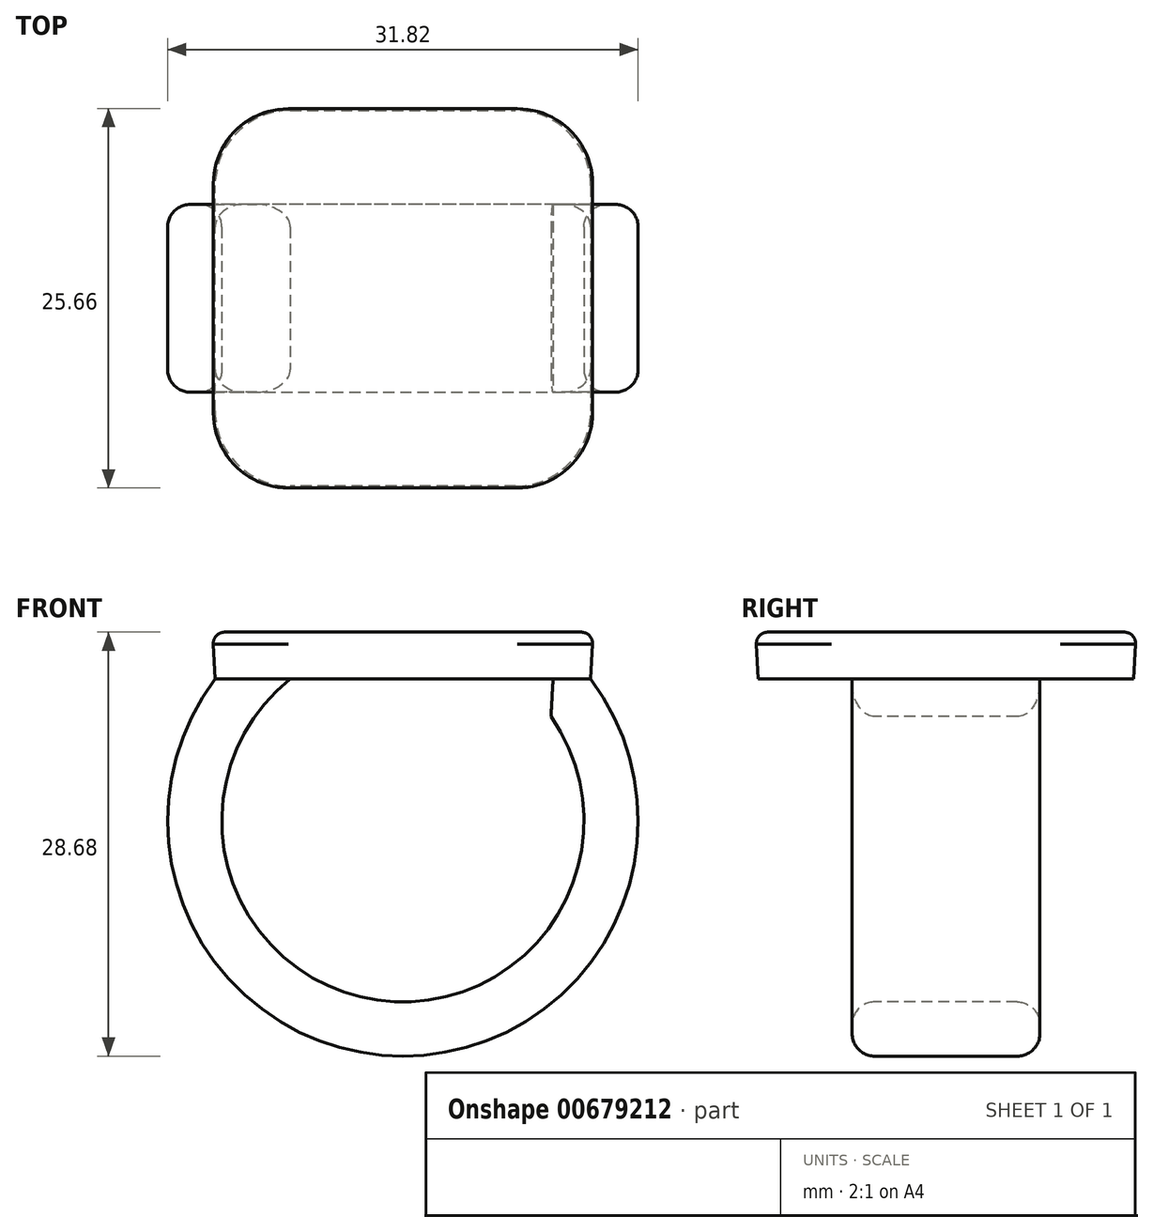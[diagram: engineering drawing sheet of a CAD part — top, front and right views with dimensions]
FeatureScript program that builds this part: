
annotation { "Feature Type Name" : "Feature", "Feature Type Description" : "" }
export const myFeature = defineFeature(function(context is Context, id is Id, definition is map)
    precondition{}
    {
        {
            var Q0;
            Q0=qCreatedBy(makeId("Top.planeOp"),FACE);
            var sketch = newSketch(context, id + "F0", { "sketchPlane" : qUnion([Q0])});
            skLineSegment(sketch, "E0.bottom", {"start": v(12.7, 12.7) * mm, "end": v(-12.7, 12.7) * mm});
            skLineSegment(sketch, "E0.top", {"start": v(12.7, -12.7) * mm, "end": v(-12.7, -12.7) * mm});
            skLineSegment(sketch, "E0.left", {"start": v(12.7, 12.7) * mm, "end": v(12.7, -12.7) * mm});
            skLineSegment(sketch, "E0.right", {"start": v(-12.7, 12.7) * mm, "end": v(-12.7, -12.7) * mm});
            skPoint(sketch, "E0.middle", {"position": v(0, 0) * mm});
            skSolve(sketch);
        }
        {
            var Q0;
            Q0=makeQuery(id+"F0.imprint","IMPRINT",FACE,{"disambiguationData":[TD([[makeQuery(id+"F0.imprint","IMPRINT",EDGE,{"derivedFrom":sQuery(id+"F0.wireOp",EDGE,"E0.bottom")}),1.0]])]});
            extrude(context, id + "F1", {"entities" : qUnion([Q0]), "depth" : 3.17 * mm, "offsetDistance" : 25.4 * mm, "hasDraft" : true, "draftAngle" : 3 * degree});
        }
        {
            var Q0;
            Q0=qCreatedBy(makeId("Front.planeOp"),FACE);
            var sketch = newSketch(context, id + "F2", { "sketchPlane" : qUnion([Q0])});
            skArc(sketch, "E1", {"start": v(-10.16, 0) * mm, "mid": v(0, -23.56) * mm, "end": v(10.16, 0) * mm});
            skSolve(sketch);
        }
        {
            var Q0;
            Q0=makeQuery(id+"F1.opExtrude","CAP_FACE",FACE,{"disambiguationData":[OSD([sQuery(id+"F0.wireOp",EDGE,"E0.bottom"),sQuery(id+"F0.wireOp",EDGE,"E0.top"),sQuery(id+"F0.wireOp",EDGE,"E0.left"),sQuery(id+"F0.wireOp",EDGE,"E0.right")])],"isStart":true});
            var sketch = newSketch(context, id + "F3", { "sketchPlane" : qUnion([Q0])});
            skLineSegment(sketch, "E2.bottom", {"start": v(-7.62, -6.35) * mm, "end": v(-12.7, -6.35) * mm});
            skLineSegment(sketch, "E2.top", {"start": v(-7.62, 6.35) * mm, "end": v(-12.7, 6.35) * mm});
            skLineSegment(sketch, "E2.left", {"start": v(-7.62, -6.35) * mm, "end": v(-7.62, 6.35) * mm});
            skLineSegment(sketch, "E2.right", {"start": v(-12.7, -6.35) * mm, "end": v(-12.7, 6.35) * mm});
            skPoint(sketch, "E2.middle", {"position": v(-10.16, 0) * mm});
            skSolve(sketch);
        }
        {
            var Q0;
            Q0 = qSketchRegion(id + "F3", true);
            var Q1;
            Q1 = qConstructionFilter(qBodyType(qCreatedBy(id + "F2" ,EDGE), BodyType.WIRE), ConstructionObject.NO);
            sweep(context, id + "F4", {"operationType" : NewBodyOperationType.ADD, "profiles" : qUnion([Q0]), "path" : qUnion([Q1])});
        }
        {
            var Q0;
            Q0=makeQuery(id+"F1.opExtrude","SWEPT_EDGE",EDGE,{"disambiguationData":[OSD([sQuery(id+"F0.wireOp",EDGE,"E0.top"),sQuery(id+"F0.wireOp",EDGE,"E0.left")])]});
            var Q1;
            Q1=makeQuery(id+"F1.opExtrude","SWEPT_EDGE",EDGE,{"disambiguationData":[OSD([sQuery(id+"F0.wireOp",EDGE,"E0.top"),sQuery(id+"F0.wireOp",EDGE,"E0.right")])]});
            var Q2;
            Q2=makeQuery(id+"F1.opExtrude","SWEPT_EDGE",EDGE,{"disambiguationData":[OSD([sQuery(id+"F0.wireOp",EDGE,"E0.bottom"),sQuery(id+"F0.wireOp",EDGE,"E0.right")])]});
            var Q3;
            Q3=makeQuery(id+"F1.opExtrude","SWEPT_EDGE",EDGE,{"disambiguationData":[OSD([sQuery(id+"F0.wireOp",EDGE,"E0.bottom"),sQuery(id+"F0.wireOp",EDGE,"E0.left")])]});
            fillet(context, id + "F5", {"entities" : qUnion([Q0, Q1, Q2, Q3]), "radius" : 5.08 * mm, "tangentPropagation" : true, "allowEdgeOverflow" : false});
        }
        {
            var Q0;
            Q0=makeQuery(id+"F4.opSweep","SWEPT_EDGE",EDGE,{"disambiguationData":[OSD([sQuery(id+"F0.wireOp",EDGE,"E0.right"),sQuery(id+"F2.wireOp",EDGE,"E1"),sQuery(id+"F3.wireOp",EDGE,"E2.bottom"),sQuery(id+"F3.wireOp",EDGE,"E2.right")])]});
            var Q1;
            Q1=makeQuery(id+"F4.opSweep","SWEPT_EDGE",EDGE,{"disambiguationData":[OSD([sQuery(id+"F0.wireOp",EDGE,"E0.right"),sQuery(id+"F2.wireOp",EDGE,"E1"),sQuery(id+"F3.wireOp",EDGE,"E2.top"),sQuery(id+"F3.wireOp",EDGE,"E2.right")])]});
            var Q2;
            Q2=makeQuery(id+"F4.opSweep","SWEPT_EDGE",EDGE,{"disambiguationData":[OSD([sQuery(id+"F2.wireOp",EDGE,"E1"),sQuery(id+"F3.wireOp",EDGE,"E2.top"),sQuery(id+"F3.wireOp",EDGE,"E2.left")])]});
            var Q3;
            Q3=makeQuery(id+"F4.opSweep","SWEPT_EDGE",EDGE,{"disambiguationData":[OSD([sQuery(id+"F2.wireOp",EDGE,"E1"),sQuery(id+"F3.wireOp",EDGE,"E2.bottom"),sQuery(id+"F3.wireOp",EDGE,"E2.left")])]});
            fillet(context, id + "F6", {"entities" : qUnion([Q0, Q1, Q2, Q3]), "radius" : 1.52 * mm, "tangentPropagation" : true, "allowEdgeOverflow" : false});
        }
        {
            var Q0;
            Q0=makeQuery(id+"F1.opExtrude","CAP_FACE",FACE,{"disambiguationData":[OSD([sQuery(id+"F0.wireOp",EDGE,"E0.bottom"),sQuery(id+"F0.wireOp",EDGE,"E0.top"),sQuery(id+"F0.wireOp",EDGE,"E0.left"),sQuery(id+"F0.wireOp",EDGE,"E0.right")])],"isStart":false});
            fillet(context, id + "F7", {"entities" : qUnion([Q0]), "radius" : 0.76 * mm, "tangentPropagation" : true, "allowEdgeOverflow" : false});
        }
    });
